# Revit family: 210_2d41d34e66ac4bf3b519fc2583c610
name_source: partatom
category: Duct Accessories
units: mm (PartAtom-declared; Revit-internal decimal feet)

## family parameters
Always vertical = Yes
Cut with Voids When Loaded = No
Part Type = Breaks Into
Round Connector Dimension = Use Diameter
Shared = No
Work Plane-Based = No

## types (7) — shared parameters
CAT0 = Yes
D12 = 2 mm  [stored 0.00656168 ft]
D13 = 2 mm  [stored 0.00656168 ft]
Description = VENTILATOR
F1 = 8 mm  [stored 0.0262467 ft]
F12 = 4 mm  [stored 0.0131234 ft]
LB3 = 10 mm  [stored 0.0328084 ft]
LB3__ve = -10 mm  [stored -0.0328084 ft]
LM1 = 5 mm  [stored 0.0164042 ft]
Manufacturer = Alnor
QmdConnectorList = 201;D;202;D
URL = http://www.ventilation-alnor.co.uk
W = 500 mm
WW = 100 mm  [stored 0.328084 ft]
magiPartTypeId = 210
magiProductFamilyId = 2d41d34e66ac4bf3b519fc2583c610

## per-type parameters (varying)
| type | D | D32 | E | F | L1 | L2 | LB1 | LB2 | LL | LM | R | R1 | RH | ZB | magiProductId |
| DV-100 | 100 mm | 119 mm | 25 mm  [stored 0.082021 ft] | 161 mm | 25 mm  [stored 0.082021 ft] | 61 mm | 61 mm | 102 mm  [stored 0.334646 ft] | 88 mm | 88 mm | 50 mm  [stored 0.164042 ft] | 50 mm  [stored 0.164042 ft] | 7 mm  [stored 0.0229659 ft] | 111 mm | 5c162534064d4887a5d195c679afd2 |
| DV-315 | 315 mm | 201 mm | 30 mm  [stored 0.0984252 ft] | 243 mm | 25 mm  [stored 0.082021 ft] | 80 mm  [stored 0.262467 ft] | 80 mm  [stored 0.262467 ft] | 133 mm | 107 mm | 126 mm | 158 mm | 158 mm | 12 mm  [stored 0.0393701 ft] | 189 mm | bb2ae37f42cd4054af1245b401fbc5 |
| DV-250 | 250 mm | 167 mm | 28 mm | 209 mm | 28 mm | 63 mm | 63 mm | 105 mm | 93 mm | 86 mm | 125 mm | 125 mm | 10 mm  [stored 0.0328084 ft] | 156 mm | 10b8ce2745c54e76afb3fb06a3b902 |
| DV-200 | 200 mm | 167 mm | 25 mm  [stored 0.082021 ft] | 209 mm | 25 mm  [stored 0.082021 ft] | 63 mm | 63 mm | 105 mm | 90 mm | 92 mm  [stored 0.301837 ft] | 100 mm  [stored 0.328084 ft] | 100 mm  [stored 0.328084 ft] | 10 mm  [stored 0.0328084 ft] | 156 mm | 258b601944454350b00ec7be1f9e01 |
| DV-160 | 160 mm | 139 mm | 25 mm  [stored 0.082021 ft] | 181 mm | 25 mm  [stored 0.082021 ft] | 59 mm | 59 mm | 98 mm  [stored 0.321522 ft] | 86 mm | 82 mm | 80 mm  [stored 0.262467 ft] | 80 mm  [stored 0.262467 ft] | 8 mm  [stored 0.0262467 ft] | 131 mm | 44b26e59f439429aad212fdc57cf71 |
| DV-150 | 150 mm | 139 mm | 25 mm  [stored 0.082021 ft] | 181 mm | 25 mm  [stored 0.082021 ft] | 59 mm | 59 mm | 98 mm  [stored 0.321522 ft] | 86 mm | 82 mm | 75 mm | 75 mm | 8 mm  [stored 0.0262467 ft] | 131 mm | 4558ee72f69e4f1e9cc0702a2a1eaf |
| DV-125 | 125 mm | 119 mm | 25 mm  [stored 0.082021 ft] | 161 mm | 25 mm  [stored 0.082021 ft] | 58 mm | 58 mm | 97 mm | 85 mm | 80 mm  [stored 0.262467 ft] | 63 mm | 63 mm | 7 mm  [stored 0.0229659 ft] | 111 mm | cbf6cd3c80d5450992daf436a09a18 |

note: column(s) folded — value = type name in every type: MC Product Code

note: [stored X ft] marks values corroborated as IEEE doubles in the binary element streams (Revit-internal decimal feet)

## geometry (parser evidence)
native form markers: Blend x4, Sweep x2
no freeform markers — native parametric forms only
